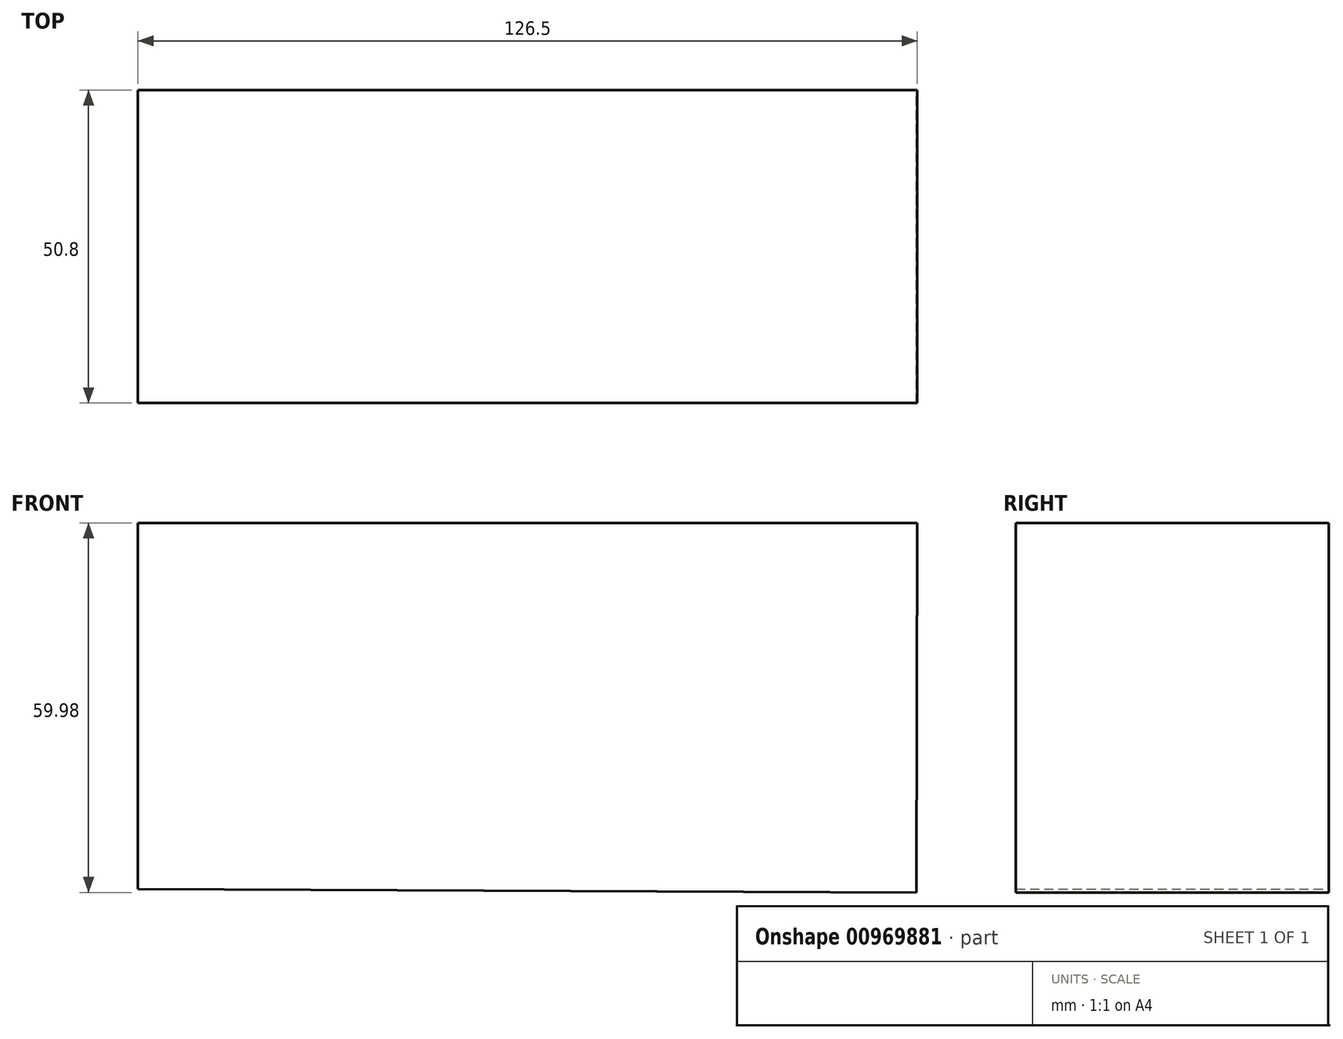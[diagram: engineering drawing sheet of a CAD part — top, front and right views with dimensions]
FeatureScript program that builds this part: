
annotation { "Feature Type Name" : "Feature", "Feature Type Description" : "" }
export const myFeature = defineFeature(function(context is Context, id is Id, definition is map)
    precondition{}
    {
        {
            var Q0;
            Q0=qCreatedBy(makeId("Front.planeOp"),FACE);
            var sketch = newSketch(context, id + "F0", { "sketchPlane" : qUnion([Q0])});
            skLineSegment(sketch, "E0", {"start": v(-66.16, 64.57) * mm, "end": v(60.34, 64.57) * mm});
            skLineSegment(sketch, "E1", {"start": v(60.34, 64.57) * mm, "end": v(60.16, 4.59) * mm});
            skLineSegment(sketch, "E2", {"start": v(60.16, 4.59) * mm, "end": v(-66.16, 5.12) * mm});
            skLineSegment(sketch, "E3", {"start": v(-66.16, 5.12) * mm, "end": v(-66.16, 64.57) * mm});
            skSolve(sketch);
        }
        {
            var Q0;
            Q0=makeQuery(id+"F0.imprint","IMPRINT",FACE,{"disambiguationData":[TD([[makeQuery(id+"F0.imprint","IMPRINT",EDGE,{"derivedFrom":sQuery(id+"F0.wireOp",EDGE,"E0")}),-1.0]])]});
            extrude(context, id + "F1", {"entities" : qUnion([Q0]), "depth" : 50.8 * mm, "offsetDistance" : 25.4 * mm});
        }
    });
